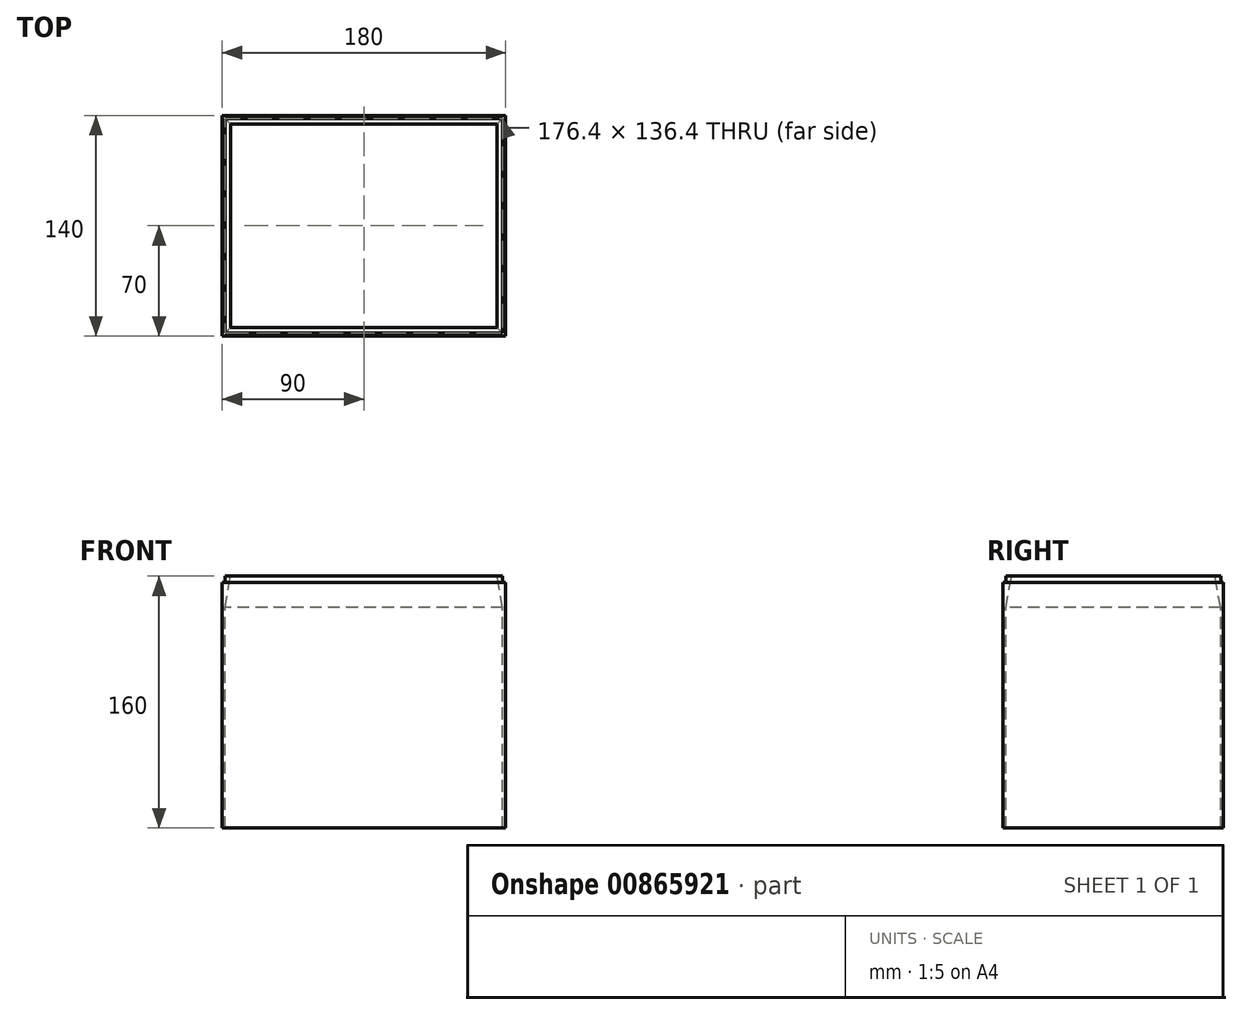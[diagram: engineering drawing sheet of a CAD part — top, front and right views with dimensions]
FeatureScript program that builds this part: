
annotation { "Feature Type Name" : "Feature", "Feature Type Description" : "" }
export const myFeature = defineFeature(function(context is Context, id is Id, definition is map)
    precondition{}
    {
        {
            var Q0;
            Q0=qCreatedBy(makeId("Top.planeOp"),FACE);
            var sketch = newSketch(context, id + "F0", { "sketchPlane" : qUnion([Q0])});
            skLineSegment(sketch, "E0.bottom", {"start": v(90, 70) * mm, "end": v(-90, 70) * mm});
            skLineSegment(sketch, "E0.top", {"start": v(90, -70) * mm, "end": v(-90, -70) * mm});
            skLineSegment(sketch, "E0.left", {"start": v(90, 70) * mm, "end": v(90, -70) * mm});
            skLineSegment(sketch, "E0.right", {"start": v(-90, 70) * mm, "end": v(-90, -70) * mm});
            skPoint(sketch, "E0.middle", {"position": v(0, 0) * mm});
            skSolve(sketch);
        }
        {
            var Q0;
            Q0=qCreatedBy(makeId("Top.planeOp"),FACE);
            var sketch = newSketch(context, id + "F1", { "sketchPlane" : qUnion([Q0])});
            skLineSegment(sketch, "E1.bottom", {"start": v(88.2, 68.2) * mm, "end": v(-88.2, 68.2) * mm});
            skLineSegment(sketch, "E1.top", {"start": v(88.2, -68.2) * mm, "end": v(-88.2, -68.2) * mm});
            skLineSegment(sketch, "E1.left", {"start": v(88.2, 68.2) * mm, "end": v(88.2, -68.2) * mm});
            skLineSegment(sketch, "E1.right", {"start": v(-88.2, 68.2) * mm, "end": v(-88.2, -68.2) * mm});
            skPoint(sketch, "E1.middle", {"position": v(0, 0) * mm});
            skSolve(sketch);
        }
        {
            var Q0;
            Q0=qCreatedBy(makeId("Top.planeOp"),FACE);
            cPlane(context, id + "F2", {"entities" : qUnion([Q0]), "cplaneType" : CPlaneType.OFFSET, "offset" : 20 * mm, "width" : 150 * mm, "height" : 150 * mm});
        }
        {
            var Q0;
            Q0=qCreatedBy(id+"F2.planeOp",FACE);
            var sketch = newSketch(context, id + "F3", { "sketchPlane" : qUnion([Q0])});
            skLineSegment(sketch, "E2.0", {"start": v(-90, 70) * mm, "end": v(-90, -70) * mm});
            skLineSegment(sketch, "E2.1", {"start": v(90, 70) * mm, "end": v(-90, 70) * mm});
            skLineSegment(sketch, "E2.2", {"start": v(90, 70) * mm, "end": v(90, -70) * mm});
            skLineSegment(sketch, "E2.3", {"start": v(90, -70) * mm, "end": v(-90, -70) * mm});
            skSolve(sketch);
        }
        {
            var Q0;
            Q0=qCreatedBy(id+"F2.planeOp",FACE);
            var sketch = newSketch(context, id + "F4", { "sketchPlane" : qUnion([Q0])});
            skLineSegment(sketch, "E3.bottom", {"start": v(84.6, 64.6) * mm, "end": v(-84.6, 64.6) * mm});
            skLineSegment(sketch, "E3.top", {"start": v(84.6, -64.6) * mm, "end": v(-84.6, -64.6) * mm});
            skLineSegment(sketch, "E3.left", {"start": v(84.6, 64.6) * mm, "end": v(84.6, -64.6) * mm});
            skLineSegment(sketch, "E3.right", {"start": v(-84.6, 64.6) * mm, "end": v(-84.6, -64.6) * mm});
            skPoint(sketch, "E3.middle", {"position": v(0, 0) * mm});
            skSolve(sketch);
        }
        {
            var Q0;
            Q0=makeQuery(id+"F1.imprint","IMPRINT",FACE,{"disambiguationData":[TD([[makeQuery(id+"F1.imprint","IMPRINT",EDGE,{"derivedFrom":sQuery(id+"F1.wireOp",EDGE,"E1.bottom")}),1.0]])]});
            var Q1;
            Q1=makeQuery(id+"F4.imprint","IMPRINT",FACE,{"disambiguationData":[TD([[makeQuery(id+"F4.imprint","IMPRINT",EDGE,{"derivedFrom":sQuery(id+"F4.wireOp",EDGE,"E3.bottom")}),1.0]])]});
            loft(context, id + "F5", {"sheetProfilesArray" : [{ "sheetProfileEntities" : qUnion([Q0]) }, { "sheetProfileEntities" : qUnion([Q1]) }]});
        }
        {
            var Q0;
            Q0=makeQuery(id+"F0.imprint","IMPRINT",FACE,{"disambiguationData":[TD([[makeQuery(id+"F0.imprint","IMPRINT",EDGE,{"derivedFrom":sQuery(id+"F0.wireOp",EDGE,"E0.bottom")}),1.0]])]});
            var Q1;
            Q1=makeQuery(id+"F3.imprint","IMPRINT",FACE,{"disambiguationData":[TD([[makeQuery(id+"F3.imprint","IMPRINT",EDGE,{"derivedFrom":sQuery(id+"F3.wireOp",EDGE,"E2.0")}),1.0]])]});
            loft(context, id + "F6", {"sheetProfilesArray" : [{ "sheetProfileEntities" : qUnion([Q0]) }, { "sheetProfileEntities" : qUnion([Q1]) }]});
        }
        {
            var Q0;
            Q0=makeQuery(id+"F5.opLoft","SWEPT_BODY",BODY,{"disambiguationData":[OSD([makeQuery(id+"F1.imprint","IMPRINT",FACE,{"disambiguationData":[TD([[makeQuery(id+"F1.imprint","IMPRINT",EDGE,{"derivedFrom":sQuery(id+"F1.wireOp",EDGE,"E1.bottom")}),1.0]])]}),makeQuery(id+"F4.imprint","IMPRINT",FACE,{"disambiguationData":[TD([[makeQuery(id+"F4.imprint","IMPRINT",EDGE,{"derivedFrom":sQuery(id+"F4.wireOp",EDGE,"E3.bottom")}),1.0]])]})])]});
            var Q1;
            Q1=makeQuery(id+"F6.opLoft","SWEPT_BODY",BODY,{"disambiguationData":[OSD([makeQuery(id+"F0.imprint","IMPRINT",FACE,{"disambiguationData":[TD([[makeQuery(id+"F0.imprint","IMPRINT",EDGE,{"derivedFrom":sQuery(id+"F0.wireOp",EDGE,"E0.bottom")}),1.0]])]}),makeQuery(id+"F3.imprint","IMPRINT",FACE,{"disambiguationData":[TD([[makeQuery(id+"F3.imprint","IMPRINT",EDGE,{"derivedFrom":sQuery(id+"F3.wireOp",EDGE,"E2.0")}),1.0]])]})])]});
            booleanBodies(context, id + "F7", {"operationType" : BooleanOperationType.SUBTRACTION, "tools" : qUnion([Q0]), "targets" : qUnion([Q1])});
        }
        {
            var Q0;
            Q0=makeQuery(id+"F6.opLoft","CAP_FACE",FACE,{"disambiguationData":[OSD([makeQuery(id+"F3.imprint","IMPRINT",FACE,{"disambiguationData":[TD([[makeQuery(id+"F3.imprint","IMPRINT",EDGE,{"derivedFrom":sQuery(id+"F3.wireOp",EDGE,"E2.0")}),1.0]])]})])],"isStart":true});
            var sketch = newSketch(context, id + "F8", { "sketchPlane" : qUnion([Q0])});
            skLineSegment(sketch, "E4.0", {"start": v(90, 70) * mm, "end": v(-90, 70) * mm});
            skLineSegment(sketch, "E4.1", {"start": v(-90, 70) * mm, "end": v(-90, -70) * mm});
            skLineSegment(sketch, "E4.2", {"start": v(90, -70) * mm, "end": v(90, 70) * mm});
            skLineSegment(sketch, "E4.3", {"start": v(-90, -70) * mm, "end": v(90, -70) * mm});
            skLineSegment(sketch, "E5.0", {"start": v(88.2, 68.2) * mm, "end": v(-88.2, 68.2) * mm});
            skLineSegment(sketch, "E5.1", {"start": v(-88.2, 68.2) * mm, "end": v(-88.2, -68.2) * mm});
            skLineSegment(sketch, "E5.2", {"start": v(88.2, 68.2) * mm, "end": v(88.2, -68.2) * mm});
            skLineSegment(sketch, "E5.3", {"start": v(88.2, -68.2) * mm, "end": v(-88.2, -68.2) * mm});
            skSolve(sketch);
        }
        {
            var Q0;
            Q0=makeQuery(id+"F8.imprint","IMPRINT",FACE,{"disambiguationData":[TD([[makeQuery(id+"F8.imprint","IMPRINT",EDGE,{"derivedFrom":sQuery(id+"F8.wireOp",EDGE,"E4.0")}),1.0]])]});
            extrude(context, id + "F9", {"entities" : qUnion([Q0]), "operationType" : NewBodyOperationType.REMOVE, "oppositeDirection" : true, "depth" : 4 * mm, "offsetDistance" : 25 * mm});
        }
        {
            var Q0;
            Q0=makeQuery(id+"F6.opLoft","CAP_FACE",FACE,{"disambiguationData":[OSD([makeQuery(id+"F0.imprint","IMPRINT",FACE,{"disambiguationData":[TD([[makeQuery(id+"F0.imprint","IMPRINT",EDGE,{"derivedFrom":sQuery(id+"F0.wireOp",EDGE,"E0.bottom")}),1.0]])]})])],"isStart":true});
            var sketch = newSketch(context, id + "F10", { "sketchPlane" : qUnion([Q0])});
            skSolve(sketch);
        }
        {
            var Q0;
            {var subQ0=sQuery(id+"F0.wireOp",EDGE,"E0.right");var subQ1=sQuery(id+"F0.wireOp",EDGE,"E0.left");var subQ3=sQuery(id+"F0.wireOp",EDGE,"E0.bottom");Q0=makeQuery(id+"F10.imprint","IMPRINT",FACE,{"disambiguationData":[TD([[makeQuery(id+"F10.imprint","IMPRINT",EDGE,{"derivedFrom":makeQuery(id+"F6.opLoft","MID_CAP_EDGE",EDGE,{"disambiguationData":[OSD([subQ3,subQ1,subQ0])],"capPos":0.0})}),-1.0]])]});}
            extrude(context, id + "F11", {"entities" : qUnion([Q0]), "operationType" : NewBodyOperationType.ADD, "depth" : 140 * mm, "offsetDistance" : 25 * mm});
        }
    });
